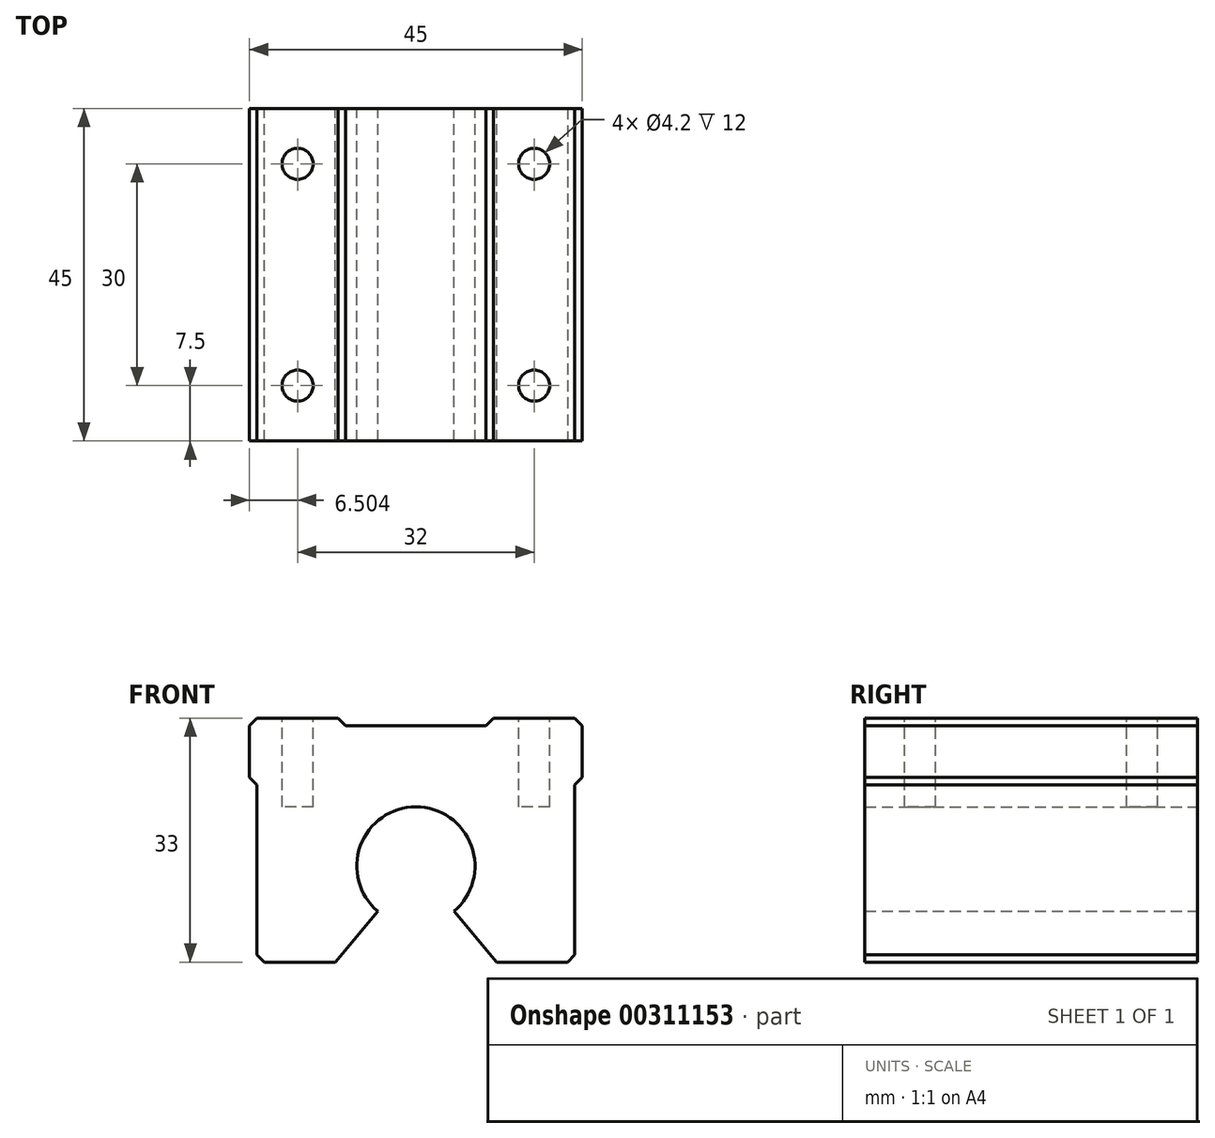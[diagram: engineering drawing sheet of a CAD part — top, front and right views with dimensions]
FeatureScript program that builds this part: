
annotation { "Feature Type Name" : "Feature", "Feature Type Description" : "" }
export const myFeature = defineFeature(function(context is Context, id is Id, definition is map)
    precondition{}
    {
        {
            var Q0;
            Q0=qCreatedBy(makeId("Front.planeOp"),FACE);
            var sketch = newSketch(context, id + "F0", { "sketchPlane" : qUnion([Q0])});
            skLineSegment(sketch, "E0", {"start": v(75.05, -30.6) * mm, "end": v(88.05, -30.6) * mm});
            skLineSegment(sketch, "E1", {"start": v(107.05, -30.6) * mm, "end": v(120.05, -30.6) * mm});
            skLineSegment(sketch, "E2", {"start": v(81.55, -30.99) * mm, "end": v(81.55, -36.3) * mm, "construction": true});
            skLineSegment(sketch, "E3", {"start": v(113.55, -30.99) * mm, "end": v(113.55, -36.3) * mm, "construction": true});
            skLineSegment(sketch, "E4", {"start": v(107.05, -31.6) * mm, "end": v(88.05, -31.6) * mm});
            skLineSegment(sketch, "E5", {"start": v(75.05, -30.6) * mm, "end": v(75.05, -39.6) * mm});
            skLineSegment(sketch, "E6", {"start": v(75.05, -39.6) * mm, "end": v(76.05, -39.6) * mm});
            skLineSegment(sketch, "E7", {"start": v(76.05, -39.6) * mm, "end": v(76.05, -63.6) * mm});
            skLineSegment(sketch, "E8", {"start": v(88.05, -30.6) * mm, "end": v(88.05, -31.6) * mm});
            skLineSegment(sketch, "E9", {"start": v(107.05, -30.6) * mm, "end": v(107.05, -31.6) * mm});
            skLineSegment(sketch, "E10", {"start": v(120.05, -30.6) * mm, "end": v(120.05, -39.6) * mm});
            skLineSegment(sketch, "E11", {"start": v(120.05, -39.6) * mm, "end": v(119.05, -39.6) * mm});
            skLineSegment(sketch, "E12", {"start": v(119.05, -39.6) * mm, "end": v(119.05, -63.6) * mm});
            skPoint(sketch, "E13.centerSnap0", {"position": v(97.55, -31.6) * mm});
            skLineSegment(sketch, "E14", {"start": v(76.05, -63.6) * mm, "end": v(86.65, -63.6) * mm});
            skLineSegment(sketch, "E15", {"start": v(119.05, -63.6) * mm, "end": v(108.46, -63.6) * mm});
            skLineSegment(sketch, "E16", {"start": v(86.65, -63.6) * mm, "end": v(92.41, -56.73) * mm});
            skLineSegment(sketch, "E17", {"start": v(108.46, -63.6) * mm, "end": v(102.7, -56.73) * mm});
            skArc(sketch, "E18", {"start": v(92.41, -56.73) * mm, "mid": v(97.55, -42.6) * mm, "end": v(102.7, -56.73) * mm});
            skArc(sketch, "E19", {"start": v(88.55, -61.32) * mm, "mid": v(97.55, -36.6) * mm, "end": v(106.55, -61.32) * mm, "construction": true});
            skSolve(sketch);
        }
        {
            var Q0;
            Q0=makeQuery(id+"F0.imprint","IMPRINT",FACE,{"disambiguationData":[TD([[makeQuery(id+"F0.imprint","IMPRINT",EDGE,{"derivedFrom":sQuery(id+"F0.wireOp",EDGE,"E0")}),-1.0]])]});
            extrude(context, id + "F1", {"entities" : qUnion([Q0]), "depth" : 45 * mm});
        }
        {
            var Q0;
            Q0=makeQuery(id+"F1.opExtrude","SWEPT_FACE",FACE,{"disambiguationData":[OSD([sQuery(id+"F0.wireOp",EDGE,"E1")])]});
            var sketch = newSketch(context, id + "F2", { "sketchPlane" : qUnion([Q0])});
            skCircle(sketch, "E20", {"center": v(81.55, -7.5) * mm, "radius": 2.1 * mm});
            skPoint(sketch, "E20.centerSnap0", {"position": v(81.55, 0) * mm});
            skCircle(sketch, "E21", {"center": v(81.55, -37.5) * mm, "radius": 2.1 * mm});
            skCircle(sketch, "E22", {"center": v(113.55, -7.5) * mm, "radius": 2.1 * mm});
            skPoint(sketch, "E22.centerSnap0", {"position": v(113.55, 0) * mm});
            skCircle(sketch, "E23", {"center": v(113.55, -37.5) * mm, "radius": 2.1 * mm});
            skPoint(sketch, "E23.centerSnap0", {"position": v(113.55, -45) * mm});
            skSolve(sketch);
        }
        {
            var Q0;
            Q0=makeQuery(id+"F2.imprint","IMPRINT",FACE,{"disambiguationData":[TD([[makeQuery(id+"F2.imprint","IMPRINT",EDGE,{"derivedFrom":sQuery(id+"F2.wireOp",EDGE,"E20")}),1.0]])]});
            var Q1;
            Q1=makeQuery(id+"F2.imprint","IMPRINT",FACE,{"disambiguationData":[TD([[makeQuery(id+"F2.imprint","IMPRINT",EDGE,{"derivedFrom":sQuery(id+"F2.wireOp",EDGE,"E21")}),1.0]])]});
            var Q2;
            Q2=makeQuery(id+"F2.imprint","IMPRINT",FACE,{"disambiguationData":[TD([[makeQuery(id+"F2.imprint","IMPRINT",EDGE,{"derivedFrom":sQuery(id+"F2.wireOp",EDGE,"E22")}),1.0]])]});
            var Q3;
            Q3=makeQuery(id+"F2.imprint","IMPRINT",FACE,{"disambiguationData":[TD([[makeQuery(id+"F2.imprint","IMPRINT",EDGE,{"derivedFrom":sQuery(id+"F2.wireOp",EDGE,"E23")}),1.0]])]});
            extrude(context, id + "F3", {"entities" : qUnion([Q0, Q1, Q2, Q3]), "operationType" : NewBodyOperationType.REMOVE, "oppositeDirection" : true, "depth" : 12 * mm});
        }
        {
            var Q0;
            Q0=makeQuery(id+"F1.opExtrude","SWEPT_EDGE",EDGE,{"disambiguationData":[OSD([sQuery(id+"F0.wireOp",EDGE,"E0"),sQuery(id+"F0.wireOp",EDGE,"E8")])]});
            var Q1;
            Q1=makeQuery(id+"F1.opExtrude","SWEPT_EDGE",EDGE,{"disambiguationData":[OSD([sQuery(id+"F0.wireOp",EDGE,"E1"),sQuery(id+"F0.wireOp",EDGE,"E9")])]});
            var Q2;
            Q2=makeQuery(id+"F1.opExtrude","SWEPT_EDGE",EDGE,{"disambiguationData":[OSD([sQuery(id+"F0.wireOp",EDGE,"E0"),sQuery(id+"F0.wireOp",EDGE,"E5")])]});
            var Q3;
            Q3=makeQuery(id+"F1.opExtrude","SWEPT_EDGE",EDGE,{"disambiguationData":[OSD([sQuery(id+"F0.wireOp",EDGE,"E5"),sQuery(id+"F0.wireOp",EDGE,"E6")])]});
            var Q4;
            Q4=makeQuery(id+"F1.opExtrude","SWEPT_EDGE",EDGE,{"disambiguationData":[OSD([sQuery(id+"F0.wireOp",EDGE,"E1"),sQuery(id+"F0.wireOp",EDGE,"E10")])]});
            var Q5;
            Q5=makeQuery(id+"F1.opExtrude","SWEPT_EDGE",EDGE,{"disambiguationData":[OSD([sQuery(id+"F0.wireOp",EDGE,"E10"),sQuery(id+"F0.wireOp",EDGE,"E11")])]});
            var Q6;
            Q6=makeQuery(id+"F1.opExtrude","SWEPT_EDGE",EDGE,{"disambiguationData":[OSD([sQuery(id+"F0.wireOp",EDGE,"E7"),sQuery(id+"F0.wireOp",EDGE,"E14")])]});
            var Q7;
            Q7=makeQuery(id+"F1.opExtrude","SWEPT_EDGE",EDGE,{"disambiguationData":[OSD([sQuery(id+"F0.wireOp",EDGE,"E12"),sQuery(id+"F0.wireOp",EDGE,"E15")])]});
            chamfer(context, id + "F4", {"entities" : qUnion([Q0, Q1, Q2, Q3, Q4, Q5, Q6, Q7]), "width" : 1 * mm, "tangentPropagation" : true});
        }
    });
